# Revit family: P500212-164
name_source: partatom
category: Lighting Fixtures
revit_build: Autodesk Revit 2014 (Build: 20130308_1515(x64)
units: mm (PartAtom-declared; Revit-internal decimal feet)

## types (1)
- P500212-164
    Apparent Load = 100 VA
    Assembly Code = D5020200
    BLUE = Paint- Hubbell - Blue
    Color Filter = 16777215
    Connector Description = Lighting Connector
    Default Elevation = 48"
    Description = Inspired by vintage automobile engines, this pendant boasts a signature star motif for added industrial character. The smooth metal shade is coated in a beautiful coastal blue finish. The shade holds a prismatic glass diffuser primed for providing optimal task lighting.
    Diameter = 17 3/8"
    Dimming Lamp Color Temperature Shift = <None>
    Fixture distribution = Direct
    Glass = Hubbell - Glass
    Gold = Hubbell - Gold
    Height = 17 5/8"
    Housing Material = Paint - Hubbell -Steel
    Lamp = A-19 or LED
    Load Classification = Lighting
    Manufacturer = Progress Lighting
    Model = P500212-164
    Photometric Web File = generic
    Power Factor = 1
    Product Documentation Link = https://hubbellcdn.com
    Product Link = https://www.hubbell.com
    Specifications = Inspired by vintage automobile engines, this pendant boasts a signature star motif for added industrial character.
The smooth metal shade is coated in a beautiful coastal blue finish.
The shade holds a prismatic glass diffuser primed for providing optimal task lighting.
Ideal for any foyer, kitchen, or dining room.
Perfect for urban industrial, farmhouse, coastal, or vintage electric settings.
Measures 17-3/8-inch width by 17-5/8-inch height.
Uses one medium base bulb that is sold separately (100w max - LED or incandescent).
Able to be fully dimmable with dimmable bulbs.
Includes installation instructions and mounting hardware.
Progress Lighting products are designed for exceptional quality, reliability, and functionality.
    Tilt Angle = 60.00°
    URL = https://www.hubbell.com
    Voltage = 120 V
    Warranty = 5 years Warranty
    Wattage Comments = 100W
    Watts = 100 W
    White = Paint - Hubbell - Matte White

## geometry (parser evidence)
native form markers: Sweep x3
no freeform markers — native parametric forms only
